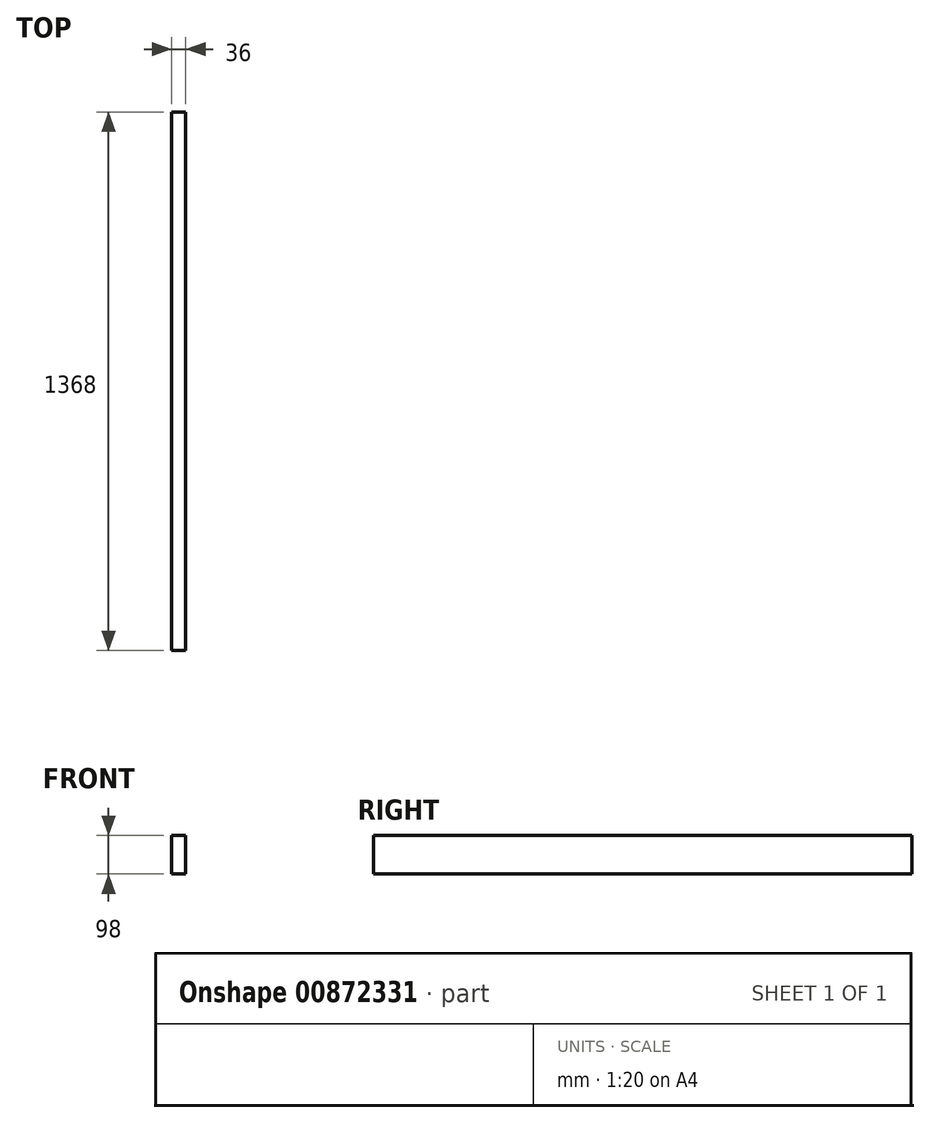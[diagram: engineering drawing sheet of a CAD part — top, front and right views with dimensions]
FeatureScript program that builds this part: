
annotation { "Feature Type Name" : "Feature", "Feature Type Description" : "" }
export const myFeature = defineFeature(function(context is Context, id is Id, definition is map)
    precondition{}
    {
        {
            var Q0;
            Q0=qCreatedBy(makeId("Front.planeOp"),FACE);
            var sketch = newSketch(context, id + "F0", { "sketchPlane" : qUnion([Q0])});
            skLineSegment(sketch, "E0.bottom", {"start": v(-18, 0) * mm, "end": v(18, 0) * mm});
            skLineSegment(sketch, "E0.top", {"start": v(-18, 98) * mm, "end": v(18, 98) * mm});
            skLineSegment(sketch, "E0.left", {"start": v(-18, 0) * mm, "end": v(-18, 98) * mm});
            skLineSegment(sketch, "E0.right", {"start": v(18, 0) * mm, "end": v(18, 98) * mm});
            skLineSegment(sketch, "E1", {"start": v(0, 0) * mm, "end": v(0, 98) * mm, "construction": true});
            skPoint(sketch, "E1.endSnap0", {"position": v(0, 98) * mm});
            skSolve(sketch);
        }
        {
            var Q0;
            Q0=makeQuery(id+"F0.imprint","IMPRINT",FACE,{"disambiguationData":[TD([[makeQuery(id+"F0.imprint","IMPRINT",EDGE,{"derivedFrom":sQuery(id+"F0.wireOp",EDGE,"E0.bottom")}),1.0]])]});
            extrude(context, id + "F1", {"entities" : qUnion([Q0]), "depth" : (1400 - 16 * 2) * mm, "offsetDistance" : 25 * mm});
        }
    });
